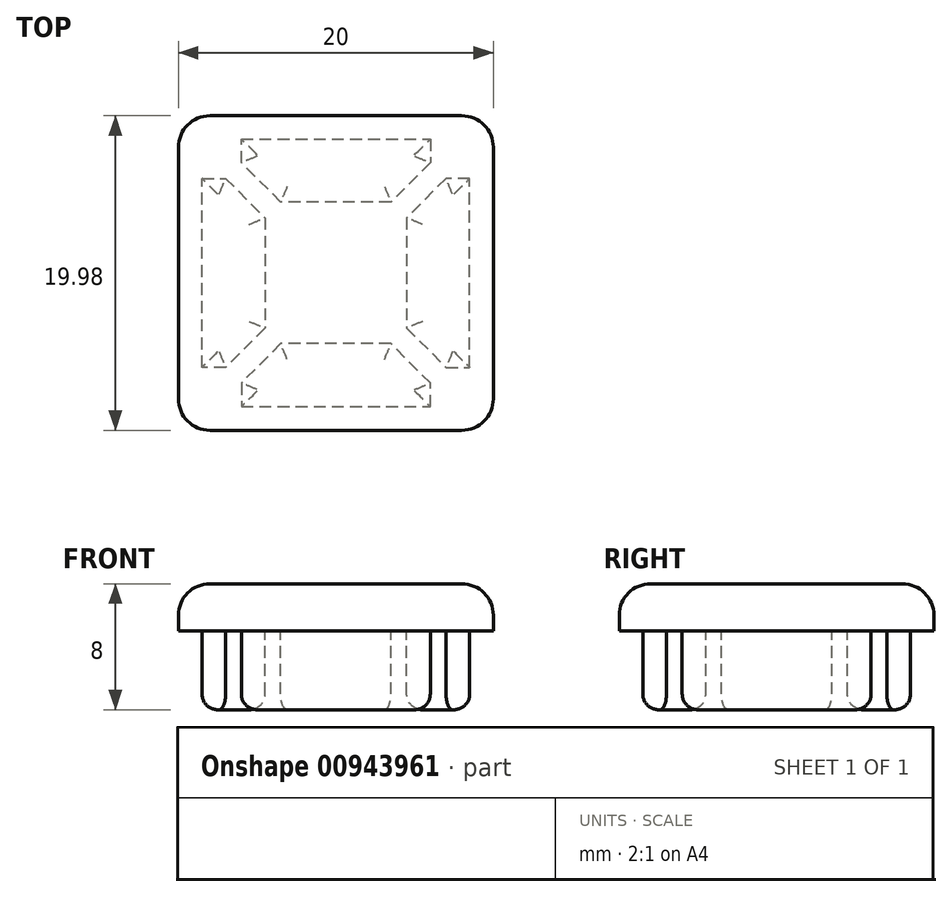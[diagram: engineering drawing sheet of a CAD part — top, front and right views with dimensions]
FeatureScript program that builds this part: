
annotation { "Feature Type Name" : "Feature", "Feature Type Description" : "" }
export const myFeature = defineFeature(function(context is Context, id is Id, definition is map)
    precondition{}
    {
        {
            var Q0;
            Q0=qCreatedBy(makeId("Top.planeOp"),FACE);
            var sketch = newSketch(context, id + "F0", { "sketchPlane" : qUnion([Q0])});
            skLineSegment(sketch, "E0.bottom", {"start": v(-8, -10) * mm, "end": v(8, -10) * mm});
            skLineSegment(sketch, "E0.top", {"start": v(-8, 10) * mm, "end": v(8, 10) * mm});
            skLineSegment(sketch, "E0.left", {"start": v(-10, -8) * mm, "end": v(-10, 8) * mm});
            skLineSegment(sketch, "E0.right", {"start": v(10, -8) * mm, "end": v(10, 8) * mm});
            skPoint(sketch, "E1.visualSharp", {"position": v(10, 10) * mm});
            skArc(sketch, "E1.filletArc", {"start": v(10, 8) * mm, "mid": v(9.41, 9.42) * mm, "end": v(8, 10) * mm});
            skPoint(sketch, "E2.visualSharp", {"position": v(-10, 10) * mm});
            skArc(sketch, "E2.filletArc", {"start": v(-8, 10) * mm, "mid": v(-9.41, 9.42) * mm, "end": v(-10, 8) * mm});
            skPoint(sketch, "E3.visualSharp", {"position": v(-10, -10) * mm});
            skArc(sketch, "E3.filletArc", {"start": v(-10, -8) * mm, "mid": v(-9.41, -9.4) * mm, "end": v(-8, -10) * mm});
            skPoint(sketch, "E4.visualSharp", {"position": v(10, -10) * mm});
            skArc(sketch, "E4.filletArc", {"start": v(8, -10) * mm, "mid": v(9.41, -9.4) * mm, "end": v(10, -8) * mm});
            skLineSegment(sketch, "E5", {"start": v(-10, -10) * mm, "end": v(10, 10) * mm, "construction": true});
            skLineSegment(sketch, "E6", {"start": v(-10, 10) * mm, "end": v(10, -10) * mm, "construction": true});
            skCircle(sketch, "E7", {"center": v(0, 0) * mm, "radius": 3 * mm});
            skCircle(sketch, "E8", {"center": v(0, 0) * mm, "radius": 2.75 * mm});
            skLineSegment(sketch, "E9.bottom", {"start": v(-2.45, -1.73) * mm, "end": v(-1.74, -2.44) * mm});
            skLineSegment(sketch, "E9.top", {"start": v(1.74, 2.45) * mm, "end": v(2.45, 1.75) * mm});
            skLineSegment(sketch, "E9.left", {"start": v(-2.45, -1.73) * mm, "end": v(1.74, 2.45) * mm});
            skLineSegment(sketch, "E9.right", {"start": v(-1.74, -2.44) * mm, "end": v(2.45, 1.75) * mm});
            skLineSegment(sketch, "E10.bottom", {"start": v(-2.45, 1.75) * mm, "end": v(-1.74, 2.45) * mm});
            skLineSegment(sketch, "E10.top", {"start": v(1.74, -2.44) * mm, "end": v(2.45, -1.73) * mm});
            skLineSegment(sketch, "E10.left", {"start": v(-2.45, 1.75) * mm, "end": v(1.74, -2.44) * mm});
            skLineSegment(sketch, "E10.right", {"start": v(-1.74, 2.45) * mm, "end": v(2.45, -1.73) * mm});
            skLineSegment(sketch, "E11", {"start": v(-3.5, 10) * mm, "end": v(-3.5, 9.5) * mm});
            skLineSegment(sketch, "E12", {"start": v(-3.5, 9.5) * mm, "end": v(-3, 9.5) * mm});
            skLineSegment(sketch, "E13", {"start": v(-3, 9.5) * mm, "end": v(-3, 8.5) * mm});
            skLineSegment(sketch, "E14", {"start": v(-3, 8.5) * mm, "end": v(-6, 8.5) * mm});
            skLineSegment(sketch, "E15", {"start": v(-6, 8.5) * mm, "end": v(-6, 7) * mm});
            skLineSegment(sketch, "E16", {"start": v(-3.5, 4.5) * mm, "end": v(-6, 7) * mm});
            skLineSegment(sketch, "E17", {"start": v(-3.5, 4.5) * mm, "end": v(3.5, 4.5) * mm});
            skLineSegment(sketch, "E18", {"start": v(3.5, 4.5) * mm, "end": v(6, 7) * mm});
            skLineSegment(sketch, "E19", {"start": v(6, 7) * mm, "end": v(6, 8.5) * mm});
            skLineSegment(sketch, "E20", {"start": v(6, 8.5) * mm, "end": v(3, 8.5) * mm});
            skLineSegment(sketch, "E21", {"start": v(3, 8.5) * mm, "end": v(3, 9.5) * mm});
            skLineSegment(sketch, "E22", {"start": v(3, 9.5) * mm, "end": v(3.5, 9.5) * mm});
            skLineSegment(sketch, "E23", {"start": v(3.5, 9.5) * mm, "end": v(3.5, 10) * mm});
            skLineSegment(sketch, "E24", {"start": v(0, 10) * mm, "end": v(0, -11.4) * mm, "construction": true});
            skLineSegment(sketch, "E25.1.0", {"start": v(-8.5, -6) * mm, "end": v(-7, -6) * mm});
            skLineSegment(sketch, "E25.1.1", {"start": v(-8.5, -3) * mm, "end": v(-8.5, -6) * mm});
            skLineSegment(sketch, "E25.1.2", {"start": v(-9.5, -3) * mm, "end": v(-8.5, -3) * mm});
            skLineSegment(sketch, "E25.1.3", {"start": v(-9.5, -3.5) * mm, "end": v(-9.5, -3) * mm});
            skLineSegment(sketch, "E25.1.4", {"start": v(-10, -3.5) * mm, "end": v(-9.5, -3.5) * mm});
            skLineSegment(sketch, "E25.1.5", {"start": v(-4.5, -3.5) * mm, "end": v(-7, -6) * mm});
            skLineSegment(sketch, "E25.1.6", {"start": v(-4.5, -3.5) * mm, "end": v(-4.5, 3.5) * mm});
            skLineSegment(sketch, "E25.1.7", {"start": v(-4.5, 3.5) * mm, "end": v(-7, 6) * mm});
            skLineSegment(sketch, "E25.1.8", {"start": v(-7, 6) * mm, "end": v(-8.5, 6) * mm});
            skLineSegment(sketch, "E25.1.9", {"start": v(-8.5, 6) * mm, "end": v(-8.5, 3) * mm});
            skLineSegment(sketch, "E25.1.10", {"start": v(-8.5, 3) * mm, "end": v(-9.5, 3) * mm});
            skLineSegment(sketch, "E25.1.11", {"start": v(-9.5, 3) * mm, "end": v(-9.5, 3.5) * mm});
            skLineSegment(sketch, "E25.1.12", {"start": v(-9.5, 3.5) * mm, "end": v(-10, 3.5) * mm});
            skLineSegment(sketch, "E25.2.0", {"start": v(6, -8.5) * mm, "end": v(6, -7) * mm});
            skLineSegment(sketch, "E25.2.1", {"start": v(3, -8.5) * mm, "end": v(6, -8.5) * mm});
            skLineSegment(sketch, "E25.2.2", {"start": v(3, -9.5) * mm, "end": v(3, -8.5) * mm});
            skLineSegment(sketch, "E25.2.3", {"start": v(3.5, -9.5) * mm, "end": v(3, -9.5) * mm});
            skLineSegment(sketch, "E25.2.4", {"start": v(3.5, -10) * mm, "end": v(3.5, -9.5) * mm});
            skLineSegment(sketch, "E25.2.5", {"start": v(3.5, -4.5) * mm, "end": v(6, -7) * mm});
            skLineSegment(sketch, "E25.2.6", {"start": v(3.5, -4.5) * mm, "end": v(-3.5, -4.5) * mm});
            skLineSegment(sketch, "E25.2.7", {"start": v(-3.5, -4.5) * mm, "end": v(-6, -7) * mm});
            skLineSegment(sketch, "E25.2.8", {"start": v(-6, -7) * mm, "end": v(-6, -8.5) * mm});
            skLineSegment(sketch, "E25.2.9", {"start": v(-6, -8.5) * mm, "end": v(-3, -8.5) * mm});
            skLineSegment(sketch, "E25.2.10", {"start": v(-3, -8.5) * mm, "end": v(-3, -9.5) * mm});
            skLineSegment(sketch, "E25.2.11", {"start": v(-3, -9.5) * mm, "end": v(-3.5, -9.5) * mm});
            skLineSegment(sketch, "E25.2.12", {"start": v(-3.5, -9.5) * mm, "end": v(-3.5, -10) * mm});
            skLineSegment(sketch, "E25.3.0", {"start": v(8.5, 6) * mm, "end": v(7, 6) * mm});
            skLineSegment(sketch, "E25.3.1", {"start": v(8.5, 3) * mm, "end": v(8.5, 6) * mm});
            skLineSegment(sketch, "E25.3.2", {"start": v(9.5, 3) * mm, "end": v(8.5, 3) * mm});
            skLineSegment(sketch, "E25.3.3", {"start": v(9.5, 3.5) * mm, "end": v(9.5, 3) * mm});
            skLineSegment(sketch, "E25.3.4", {"start": v(10, 3.5) * mm, "end": v(9.5, 3.5) * mm});
            skLineSegment(sketch, "E25.3.5", {"start": v(4.5, 3.5) * mm, "end": v(7, 6) * mm});
            skLineSegment(sketch, "E25.3.6", {"start": v(4.5, 3.5) * mm, "end": v(4.5, -3.5) * mm});
            skLineSegment(sketch, "E25.3.7", {"start": v(4.5, -3.5) * mm, "end": v(7, -6) * mm});
            skLineSegment(sketch, "E25.3.8", {"start": v(7, -6) * mm, "end": v(8.5, -6) * mm});
            skLineSegment(sketch, "E25.3.9", {"start": v(8.5, -6) * mm, "end": v(8.5, -3) * mm});
            skLineSegment(sketch, "E25.3.10", {"start": v(8.5, -3) * mm, "end": v(9.5, -3) * mm});
            skLineSegment(sketch, "E25.3.11", {"start": v(9.5, -3) * mm, "end": v(9.5, -3.5) * mm});
            skLineSegment(sketch, "E25.3.12", {"start": v(9.5, -3.5) * mm, "end": v(10, -3.5) * mm});
            skLineSegment(sketch, "E26", {"start": v(-0.5, 4.5) * mm, "end": v(0, 4) * mm});
            skLineSegment(sketch, "E27", {"start": v(0, 4) * mm, "end": v(0.5, 4.5) * mm});
            skLineSegment(sketch, "E28.1.0", {"start": v(-4, 0) * mm, "end": v(-4.5, 0.5) * mm});
            skLineSegment(sketch, "E28.1.1", {"start": v(-4.5, -0.5) * mm, "end": v(-4, 0) * mm});
            skLineSegment(sketch, "E28.2.0", {"start": v(0, -4) * mm, "end": v(-0.5, -4.5) * mm});
            skLineSegment(sketch, "E28.2.1", {"start": v(0.5, -4.5) * mm, "end": v(0, -4) * mm});
            skLineSegment(sketch, "E28.3.0", {"start": v(4, 0) * mm, "end": v(4.5, -0.5) * mm});
            skLineSegment(sketch, "E28.3.1", {"start": v(4.5, 0.5) * mm, "end": v(4, 0) * mm});
            skSolve(sketch);
        }
        {
            var Q0;
            Q0=qCreatedBy(makeId("Top.planeOp"),FACE);
            var sketch = newSketch(context, id + "F1", { "sketchPlane" : qUnion([Q0])});
            skLineSegment(sketch, "E29.0.0", {"start": v(4, 0) * mm, "end": v(4.5, 0.5) * mm, "construction": true});
            skLineSegment(sketch, "E29.0.1", {"start": v(4.5, 0.5) * mm, "end": v(4.5, 3.5) * mm, "construction": true});
            skLineSegment(sketch, "E29.0.2", {"start": v(4.5, 3.5) * mm, "end": v(7, 6) * mm, "construction": true});
            skLineSegment(sketch, "E29.0.3", {"start": v(7, 6) * mm, "end": v(8.5, 6) * mm, "construction": true});
            skLineSegment(sketch, "E29.0.4", {"start": v(8.5, 6) * mm, "end": v(8.5, 3) * mm, "construction": true});
            skLineSegment(sketch, "E29.0.5", {"start": v(8.5, 3) * mm, "end": v(9.5, 3) * mm, "construction": true});
            skLineSegment(sketch, "E29.0.6", {"start": v(9.5, 3) * mm, "end": v(9.5, 3.5) * mm, "construction": true});
            skLineSegment(sketch, "E29.0.7", {"start": v(9.5, 3.5) * mm, "end": v(10, 3.5) * mm, "construction": true});
            skLineSegment(sketch, "E29.0.8", {"start": v(10, 3.5) * mm, "end": v(10, 8) * mm, "construction": true});
            skArc(sketch, "E29.0.9", {"start": v(10, 8) * mm, "mid": v(9.41, 9.42) * mm, "end": v(8, 10) * mm, "construction": true});
            skLineSegment(sketch, "E29.0.10", {"start": v(8, 10) * mm, "end": v(3.5, 10) * mm, "construction": true});
            skLineSegment(sketch, "E29.0.11", {"start": v(3.5, 10) * mm, "end": v(3.5, 9.5) * mm, "construction": true});
            skLineSegment(sketch, "E29.0.12", {"start": v(3.5, 9.5) * mm, "end": v(3, 9.5) * mm, "construction": true});
            skLineSegment(sketch, "E29.0.13", {"start": v(3, 9.5) * mm, "end": v(3, 8.5) * mm, "construction": true});
            skLineSegment(sketch, "E29.0.14", {"start": v(3, 8.5) * mm, "end": v(6, 8.5) * mm, "construction": true});
            skLineSegment(sketch, "E29.0.15", {"start": v(6, 8.5) * mm, "end": v(6, 7) * mm, "construction": true});
            skLineSegment(sketch, "E29.0.16", {"start": v(6, 7) * mm, "end": v(3.5, 4.5) * mm, "construction": true});
            skLineSegment(sketch, "E29.0.17", {"start": v(3.5, 4.5) * mm, "end": v(0.5, 4.5) * mm, "construction": true});
            skLineSegment(sketch, "E29.0.18", {"start": v(0.5, 4.5) * mm, "end": v(0, 4) * mm, "construction": true});
            skLineSegment(sketch, "E29.0.19", {"start": v(0, 4) * mm, "end": v(-0.5, 4.5) * mm, "construction": true});
            skLineSegment(sketch, "E29.0.20", {"start": v(-0.5, 4.5) * mm, "end": v(-3.5, 4.5) * mm, "construction": true});
            skLineSegment(sketch, "E29.0.21", {"start": v(-3.5, 4.5) * mm, "end": v(-6, 7) * mm, "construction": true});
            skLineSegment(sketch, "E29.0.22", {"start": v(-6, 7) * mm, "end": v(-6, 8.5) * mm, "construction": true});
            skLineSegment(sketch, "E29.0.23", {"start": v(-6, 8.5) * mm, "end": v(-3, 8.5) * mm, "construction": true});
            skLineSegment(sketch, "E29.0.24", {"start": v(-3, 8.5) * mm, "end": v(-3, 9.5) * mm, "construction": true});
            skLineSegment(sketch, "E29.0.25", {"start": v(-3, 9.5) * mm, "end": v(-3.5, 9.5) * mm, "construction": true});
            skLineSegment(sketch, "E29.0.26", {"start": v(-3.5, 9.5) * mm, "end": v(-3.5, 10) * mm, "construction": true});
            skLineSegment(sketch, "E29.0.27", {"start": v(-3.5, 10) * mm, "end": v(-8, 10) * mm, "construction": true});
            skArc(sketch, "E29.0.28", {"start": v(-8, 10) * mm, "mid": v(-9.41, 9.42) * mm, "end": v(-10, 8) * mm, "construction": true});
            skLineSegment(sketch, "E29.0.29", {"start": v(-10, 8) * mm, "end": v(-10, 3.5) * mm, "construction": true});
            skLineSegment(sketch, "E29.0.30", {"start": v(-10, 3.5) * mm, "end": v(-9.5, 3.5) * mm, "construction": true});
            skLineSegment(sketch, "E29.0.31", {"start": v(-9.5, 3.5) * mm, "end": v(-9.5, 3) * mm, "construction": true});
            skLineSegment(sketch, "E29.0.32", {"start": v(-9.5, 3) * mm, "end": v(-8.5, 3) * mm, "construction": true});
            skLineSegment(sketch, "E29.0.33", {"start": v(-8.5, 3) * mm, "end": v(-8.5, 6) * mm, "construction": true});
            skLineSegment(sketch, "E29.0.34", {"start": v(-8.5, 6) * mm, "end": v(-7, 6) * mm, "construction": true});
            skLineSegment(sketch, "E29.0.35", {"start": v(-7, 6) * mm, "end": v(-4.5, 3.5) * mm, "construction": true});
            skLineSegment(sketch, "E29.0.36", {"start": v(-4.5, 3.5) * mm, "end": v(-4.5, 0.5) * mm, "construction": true});
            skLineSegment(sketch, "E29.0.37", {"start": v(-4.5, 0.5) * mm, "end": v(-4, 0) * mm, "construction": true});
            skLineSegment(sketch, "E29.0.38", {"start": v(-4, 0) * mm, "end": v(-4.5, -0.5) * mm, "construction": true});
            skLineSegment(sketch, "E29.0.39", {"start": v(-4.5, -0.5) * mm, "end": v(-4.5, -3.5) * mm, "construction": true});
            skLineSegment(sketch, "E29.0.40", {"start": v(-4.5, -3.5) * mm, "end": v(-7, -6) * mm, "construction": true});
            skLineSegment(sketch, "E29.0.41", {"start": v(-7, -6) * mm, "end": v(-8.5, -6) * mm, "construction": true});
            skLineSegment(sketch, "E29.0.42", {"start": v(-8.5, -6) * mm, "end": v(-8.5, -3) * mm, "construction": true});
            skLineSegment(sketch, "E29.0.43", {"start": v(-8.5, -3) * mm, "end": v(-9.5, -3) * mm, "construction": true});
            skLineSegment(sketch, "E29.0.44", {"start": v(-9.5, -3) * mm, "end": v(-9.5, -3.5) * mm, "construction": true});
            skLineSegment(sketch, "E29.0.45", {"start": v(-9.5, -3.5) * mm, "end": v(-10, -3.5) * mm, "construction": true});
            skLineSegment(sketch, "E29.0.46", {"start": v(-10, -3.5) * mm, "end": v(-10, -8) * mm, "construction": true});
            skArc(sketch, "E29.0.47", {"start": v(-10, -8) * mm, "mid": v(-9.41, -9.4) * mm, "end": v(-8, -10) * mm, "construction": true});
            skLineSegment(sketch, "E29.0.48", {"start": v(-8, -10) * mm, "end": v(-3.5, -10) * mm, "construction": true});
            skLineSegment(sketch, "E29.0.49", {"start": v(-3.5, -10) * mm, "end": v(-3.5, -9.5) * mm, "construction": true});
            skLineSegment(sketch, "E29.0.50", {"start": v(-3.5, -9.5) * mm, "end": v(-3, -9.5) * mm, "construction": true});
            skLineSegment(sketch, "E29.0.51", {"start": v(-3, -9.5) * mm, "end": v(-3, -8.5) * mm, "construction": true});
            skLineSegment(sketch, "E29.0.52", {"start": v(-3, -8.5) * mm, "end": v(-6, -8.5) * mm, "construction": true});
            skLineSegment(sketch, "E29.0.53", {"start": v(-6, -8.5) * mm, "end": v(-6, -7) * mm, "construction": true});
            skLineSegment(sketch, "E29.0.54", {"start": v(-6, -7) * mm, "end": v(-3.5, -4.5) * mm, "construction": true});
            skLineSegment(sketch, "E29.0.55", {"start": v(-3.5, -4.5) * mm, "end": v(-0.5, -4.5) * mm, "construction": true});
            skLineSegment(sketch, "E29.0.56", {"start": v(-0.5, -4.5) * mm, "end": v(0, -4) * mm, "construction": true});
            skLineSegment(sketch, "E29.0.57", {"start": v(0, -4) * mm, "end": v(0.5, -4.5) * mm, "construction": true});
            skLineSegment(sketch, "E29.0.58", {"start": v(0.5, -4.5) * mm, "end": v(3.5, -4.5) * mm, "construction": true});
            skLineSegment(sketch, "E29.0.59", {"start": v(3.5, -4.5) * mm, "end": v(6, -7) * mm, "construction": true});
            skLineSegment(sketch, "E29.0.60", {"start": v(6, -7) * mm, "end": v(6, -8.5) * mm, "construction": true});
            skLineSegment(sketch, "E29.0.61", {"start": v(6, -8.5) * mm, "end": v(3, -8.5) * mm, "construction": true});
            skLineSegment(sketch, "E29.0.62", {"start": v(3, -8.5) * mm, "end": v(3, -9.5) * mm, "construction": true});
            skLineSegment(sketch, "E29.0.63", {"start": v(3, -9.5) * mm, "end": v(3.5, -9.5) * mm, "construction": true});
            skLineSegment(sketch, "E29.0.64", {"start": v(3.5, -9.5) * mm, "end": v(3.5, -10) * mm, "construction": true});
            skLineSegment(sketch, "E29.0.65", {"start": v(3.5, -10) * mm, "end": v(8, -10) * mm, "construction": true});
            skArc(sketch, "E29.0.66", {"start": v(8, -10) * mm, "mid": v(9.41, -9.4) * mm, "end": v(10, -8) * mm, "construction": true});
            skLineSegment(sketch, "E29.0.67", {"start": v(10, -8) * mm, "end": v(10, -3.5) * mm, "construction": true});
            skLineSegment(sketch, "E29.0.68", {"start": v(10, -3.5) * mm, "end": v(9.5, -3.5) * mm, "construction": true});
            skLineSegment(sketch, "E29.0.69", {"start": v(9.5, -3.5) * mm, "end": v(9.5, -3) * mm, "construction": true});
            skLineSegment(sketch, "E29.0.70", {"start": v(9.5, -3) * mm, "end": v(8.5, -3) * mm, "construction": true});
            skLineSegment(sketch, "E29.0.71", {"start": v(8.5, -3) * mm, "end": v(8.5, -6) * mm, "construction": true});
            skLineSegment(sketch, "E29.0.72", {"start": v(8.5, -6) * mm, "end": v(7, -6) * mm, "construction": true});
            skLineSegment(sketch, "E29.0.73", {"start": v(7, -6) * mm, "end": v(4.5, -3.5) * mm, "construction": true});
            skLineSegment(sketch, "E29.0.74", {"start": v(4.5, -3.5) * mm, "end": v(4.5, -0.5) * mm, "construction": true});
            skLineSegment(sketch, "E29.0.75", {"start": v(4.5, -0.5) * mm, "end": v(4, 0) * mm, "construction": true});
            skLineSegment(sketch, "E30", {"start": v(-8.5, -6) * mm, "end": v(-7, -6) * mm, "construction": true});
            skLineSegment(sketch, "E31", {"start": v(-7, -6) * mm, "end": v(-4.5, -3.5) * mm, "construction": true});
            skLineSegment(sketch, "E32", {"start": v(-4.5, -3.5) * mm, "end": v(-4.5, 3.5) * mm, "construction": true});
            skLineSegment(sketch, "E33", {"start": v(-4.5, 3.5) * mm, "end": v(-7, 6) * mm, "construction": true});
            skLineSegment(sketch, "E34", {"start": v(-7, 6) * mm, "end": v(-8.5, 6) * mm, "construction": true});
            skLineSegment(sketch, "E35", {"start": v(-8.5, 6) * mm, "end": v(-8.5, -6) * mm, "construction": true});
            skLineSegment(sketch, "E36", {"start": v(-8.5, -6) * mm, "end": v(-8.5, 6) * mm});
            skLineSegment(sketch, "E37", {"start": v(-8.5, 6) * mm, "end": v(-7, 6) * mm});
            skLineSegment(sketch, "E38", {"start": v(-7, 6) * mm, "end": v(-4.5, 3.5) * mm});
            skLineSegment(sketch, "E39", {"start": v(-4.5, 3.5) * mm, "end": v(-4.5, -3.5) * mm});
            skLineSegment(sketch, "E40", {"start": v(-4.5, -3.5) * mm, "end": v(-7, -6) * mm});
            skLineSegment(sketch, "E41", {"start": v(-7, -6) * mm, "end": v(-8.5, -6) * mm});
            skLineSegment(sketch, "E42", {"start": v(-6, 8.5) * mm, "end": v(6, 8.5) * mm});
            skLineSegment(sketch, "E43", {"start": v(6, 8.5) * mm, "end": v(6, 7) * mm});
            skLineSegment(sketch, "E44", {"start": v(6, 7) * mm, "end": v(3.5, 4.5) * mm});
            skLineSegment(sketch, "E45", {"start": v(3.5, 4.5) * mm, "end": v(-3.5, 4.5) * mm});
            skLineSegment(sketch, "E46", {"start": v(-3.5, 4.5) * mm, "end": v(-6, 7) * mm});
            skLineSegment(sketch, "E47", {"start": v(-6, 7) * mm, "end": v(-6, 8.5) * mm});
            skLineSegment(sketch, "E48", {"start": v(8.5, -6) * mm, "end": v(8.5, 6) * mm});
            skLineSegment(sketch, "E49", {"start": v(8.5, 6) * mm, "end": v(7, 6) * mm});
            skLineSegment(sketch, "E50", {"start": v(7, 6) * mm, "end": v(4.5, 3.5) * mm});
            skLineSegment(sketch, "E51", {"start": v(4.5, 3.5) * mm, "end": v(4.5, -3.5) * mm});
            skLineSegment(sketch, "E52", {"start": v(4.5, -3.5) * mm, "end": v(7, -6) * mm});
            skLineSegment(sketch, "E53", {"start": v(7, -6) * mm, "end": v(8.5, -6) * mm});
            skLineSegment(sketch, "E54", {"start": v(-6, -8.5) * mm, "end": v(6, -8.5) * mm});
            skLineSegment(sketch, "E55", {"start": v(6, -8.5) * mm, "end": v(6, -7) * mm});
            skLineSegment(sketch, "E56", {"start": v(6, -7) * mm, "end": v(3.5, -4.5) * mm});
            skLineSegment(sketch, "E57", {"start": v(3.5, -4.5) * mm, "end": v(-3.5, -4.5) * mm});
            skLineSegment(sketch, "E58", {"start": v(-3.5, -4.5) * mm, "end": v(-6, -7) * mm});
            skLineSegment(sketch, "E59", {"start": v(-6, -7) * mm, "end": v(-6, -8.5) * mm});
            skSolve(sketch);
        }
        {
            var Q0;
            Q0=qCreatedBy(makeId("Top.planeOp"),FACE);
            var sketch = newSketch(context, id + "F2", { "sketchPlane" : qUnion([Q0])});
            skLineSegment(sketch, "E60.bottom", {"start": v(10, -10) * mm, "end": v(-10, -10) * mm});
            skLineSegment(sketch, "E60.top", {"start": v(10, 10) * mm, "end": v(-10, 10) * mm});
            skLineSegment(sketch, "E60.left", {"start": v(10, -10) * mm, "end": v(10, 10) * mm});
            skLineSegment(sketch, "E60.right", {"start": v(-10, -10) * mm, "end": v(-10, 10) * mm});
            skPoint(sketch, "E60.middle", {"position": v(0, 0) * mm});
            skSolve(sketch);
        }
        {
            var Q0;
            Q0=makeQuery(id+"F2.imprint","IMPRINT",FACE,{"disambiguationData":[TD([[makeQuery(id+"F2.imprint","IMPRINT",EDGE,{"derivedFrom":sQuery(id+"F2.wireOp",EDGE,"E60.bottom")}),-1.0]])]});
            extrude(context, id + "F3", {"entities" : qUnion([Q0]), "depth" : 3 * mm, "offsetDistance" : 25 * mm});
        }
        {
            var Q0;
            Q0 = qSketchRegion(id + "F1", true);
            extrude(context, id + "F4", {"entities" : qUnion([Q0]), "operationType" : NewBodyOperationType.ADD, "oppositeDirection" : true, "depth" : 5 * mm, "offsetDistance" : 25 * mm});
        }
        {
            var Q0;
            Q0=makeQuery(id+"F4.opExtrude","CAP_FACE",FACE,{"disambiguationData":[OSD([sQuery(id+"F1.wireOp",EDGE,"E42"),sQuery(id+"F1.wireOp",EDGE,"E43"),sQuery(id+"F1.wireOp",EDGE,"E44"),sQuery(id+"F1.wireOp",EDGE,"E45"),sQuery(id+"F1.wireOp",EDGE,"E46"),sQuery(id+"F1.wireOp",EDGE,"E47")])],"isStart":false});
            var Q1;
            Q1=makeQuery(id+"F4.opExtrude","CAP_FACE",FACE,{"disambiguationData":[OSD([sQuery(id+"F1.wireOp",EDGE,"E36"),sQuery(id+"F1.wireOp",EDGE,"E37"),sQuery(id+"F1.wireOp",EDGE,"E38"),sQuery(id+"F1.wireOp",EDGE,"E39"),sQuery(id+"F1.wireOp",EDGE,"E40"),sQuery(id+"F1.wireOp",EDGE,"E41")])],"isStart":false});
            var Q2;
            Q2=makeQuery(id+"F4.opExtrude","CAP_FACE",FACE,{"disambiguationData":[OSD([sQuery(id+"F1.wireOp",EDGE,"E54"),sQuery(id+"F1.wireOp",EDGE,"E55"),sQuery(id+"F1.wireOp",EDGE,"E56"),sQuery(id+"F1.wireOp",EDGE,"E57"),sQuery(id+"F1.wireOp",EDGE,"E58"),sQuery(id+"F1.wireOp",EDGE,"E59")])],"isStart":false});
            var Q3;
            Q3=makeQuery(id+"F4.opExtrude","CAP_FACE",FACE,{"disambiguationData":[OSD([sQuery(id+"F1.wireOp",EDGE,"E48"),sQuery(id+"F1.wireOp",EDGE,"E49"),sQuery(id+"F1.wireOp",EDGE,"E50"),sQuery(id+"F1.wireOp",EDGE,"E51"),sQuery(id+"F1.wireOp",EDGE,"E52"),sQuery(id+"F1.wireOp",EDGE,"E53")])],"isStart":false});
            fillet(context, id + "F5", {"entities" : qUnion([Q0, Q1, Q2, Q3]), "radius" : 1 * mm, "tangentPropagation" : true, "allowEdgeOverflow" : false});
        }
        {
            var Q0;
            Q0=makeQuery(id+"F3.opExtrude","SWEPT_EDGE",EDGE,{"disambiguationData":[OSD([sQuery(id+"F2.wireOp",EDGE,"E60.top"),sQuery(id+"F2.wireOp",EDGE,"E60.left")])]});
            var Q1;
            Q1=makeQuery(id+"F3.opExtrude","SWEPT_EDGE",EDGE,{"disambiguationData":[OSD([sQuery(id+"F2.wireOp",EDGE,"E60.bottom"),sQuery(id+"F2.wireOp",EDGE,"E60.left")])]});
            var Q2;
            Q2=makeQuery(id+"F3.opExtrude","SWEPT_EDGE",EDGE,{"disambiguationData":[OSD([sQuery(id+"F2.wireOp",EDGE,"E60.bottom"),sQuery(id+"F2.wireOp",EDGE,"E60.right")])]});
            var Q3;
            Q3=makeQuery(id+"F3.opExtrude","SWEPT_EDGE",EDGE,{"disambiguationData":[OSD([sQuery(id+"F2.wireOp",EDGE,"E60.top"),sQuery(id+"F2.wireOp",EDGE,"E60.right")])]});
            fillet(context, id + "F6", {"entities" : qUnion([Q0, Q1, Q2, Q3]), "radius" : 2 * mm, "tangentPropagation" : true, "allowEdgeOverflow" : false});
        }
        {
            var Q0;
            Q0=makeQuery(id+"F3.opExtrude","CAP_FACE",FACE,{"disambiguationData":[OSD([sQuery(id+"F2.wireOp",EDGE,"E60.bottom"),sQuery(id+"F2.wireOp",EDGE,"E60.top"),sQuery(id+"F2.wireOp",EDGE,"E60.left"),sQuery(id+"F2.wireOp",EDGE,"E60.right")])],"isStart":false});
            fillet(context, id + "F7", {"entities" : qUnion([Q0]), "radius" : 2 * mm, "tangentPropagation" : true, "allowEdgeOverflow" : false});
        }
    });
